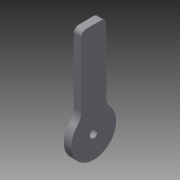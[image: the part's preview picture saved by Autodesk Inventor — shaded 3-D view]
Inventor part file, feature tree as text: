
AUTODESK INVENTOR PART (.ipt)
format: ipt  version: 2013 (Build 170138000, 138)  size: 93,696 bytes
history: native  units: mm
features: extrude x1, sketch x1
ambient origin geometry x8: Origin, YZ Plane, XZ Plane, XY Plane, X Axis, Y Axis, Z Axis, Center Point
feature tree (2):
  extrude  "Extrusion6"  Depth=3.0mm
  sketch  "Sketch1"  dims[d8=22.5deg d16=3.0mm d25=10.0mm d69=6.0mm d70=38.0mm d74=22.5deg d81=90.0mm d101=3.0mm d106=3.0mm d107=0.0mm d108=9.0mm d109=38.0mm d110=5.0mm d111=2.0mm]
